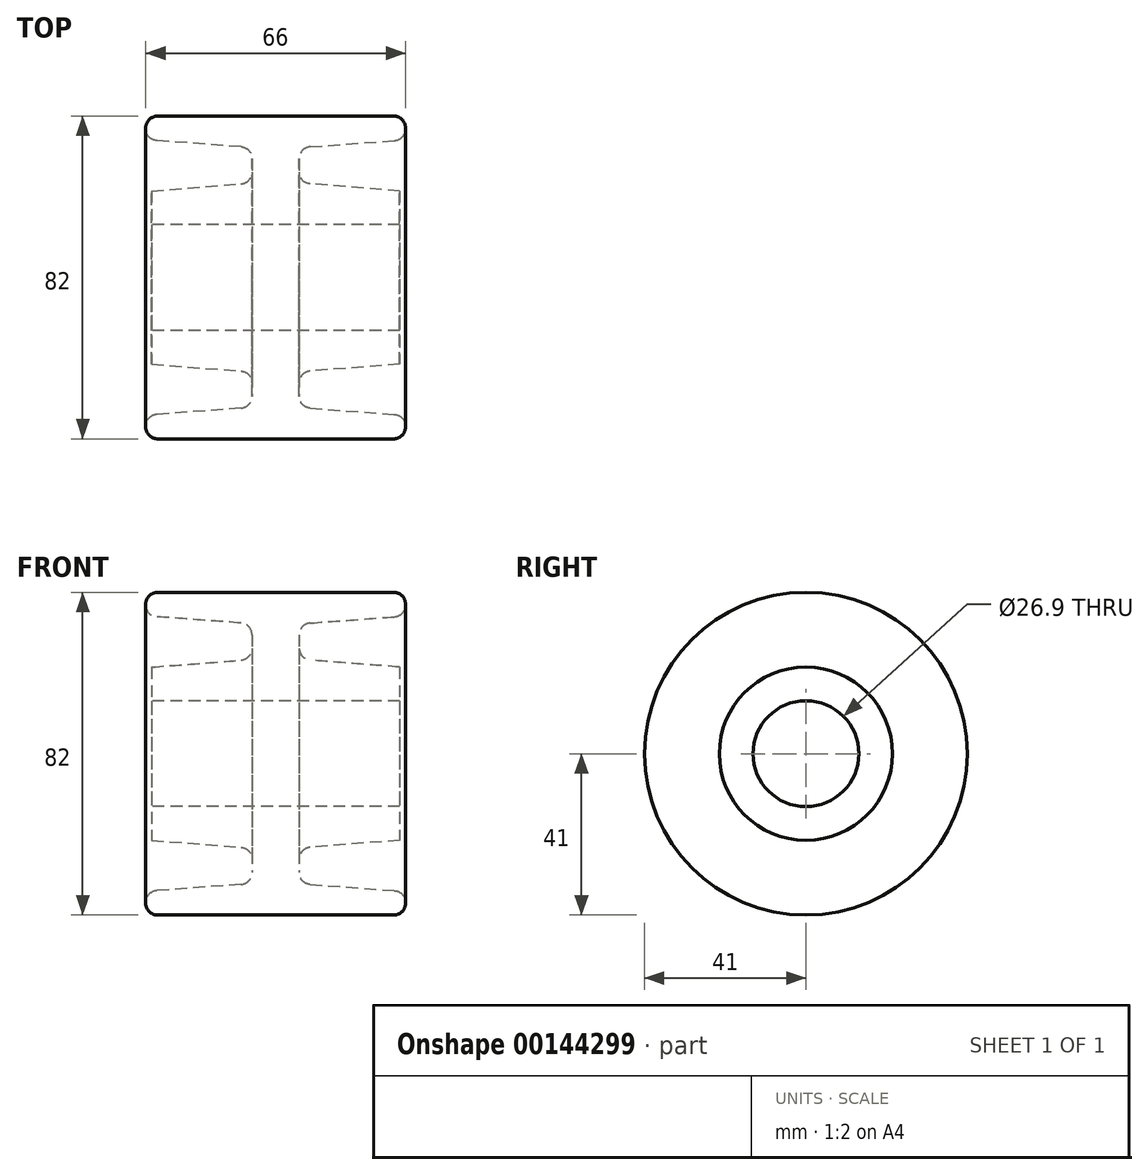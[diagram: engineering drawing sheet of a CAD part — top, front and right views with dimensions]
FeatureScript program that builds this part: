
annotation { "Feature Type Name" : "Feature", "Feature Type Description" : "" }
export const myFeature = defineFeature(function(context is Context, id is Id, definition is map)
    precondition{}
    {
        {
            var Q0;
            Q0=qCreatedBy(makeId("Front.planeOp"),FACE);
            var sketch = newSketch(context, id + "F0", { "sketchPlane" : qUnion([Q0])});
            skLineSegment(sketch, "E0", {"start": v(-24.5, 0) * mm, "end": v(76.5, 0) * mm, "construction": true});
            skLineSegment(sketch, "E1", {"start": v(64.5, 13.45) * mm, "end": v(64.5, 22) * mm});
            skLineSegment(sketch, "E2", {"start": v(64.5, 22) * mm, "end": v(41.77, 23.78) * mm});
            skLineSegment(sketch, "E3", {"start": v(39, 26.77) * mm, "end": v(39, 30.21) * mm});
            skLineSegment(sketch, "E4", {"start": v(66, 37.79) * mm, "end": v(66, 38) * mm});
            skLineSegment(sketch, "E5", {"start": v(63, 41) * mm, "end": v(3, 41) * mm});
            skLineSegment(sketch, "E6", {"start": v(27, 30.21) * mm, "end": v(27, 26.77) * mm});
            skLineSegment(sketch, "E7", {"start": v(24.23, 23.78) * mm, "end": v(1.5, 22) * mm});
            skLineSegment(sketch, "E8", {"start": v(1.5, 22) * mm, "end": v(1.5, 13.45) * mm});
            skLineSegment(sketch, "E9", {"start": v(1.5, 13.45) * mm, "end": v(64.5, 13.45) * mm});
            skLineSegment(sketch, "E10", {"start": v(33, 42.82) * mm, "end": v(33, -16.3) * mm, "construction": true});
            skLineSegment(sketch, "E11", {"start": v(0, 37.79) * mm, "end": v(0, 38) * mm});
            skLineSegment(sketch, "E12", {"start": v(2.78, 34.8) * mm, "end": v(24.22, 33.2) * mm});
            skLineSegment(sketch, "E13", {"start": v(41.78, 33.2) * mm, "end": v(63.22, 34.8) * mm});
            skPoint(sketch, "E14.visualSharp", {"position": v(0, 35) * mm});
            skArc(sketch, "E14.filletArc", {"start": v(0, 37.79) * mm, "mid": v(0.8, 35.74) * mm, "end": v(2.78, 34.8) * mm});
            skPoint(sketch, "E15.visualSharp", {"position": v(66, 35) * mm});
            skArc(sketch, "E15.filletArc", {"start": v(63.22, 34.8) * mm, "mid": v(65.2, 35.74) * mm, "end": v(66, 37.79) * mm});
            skPoint(sketch, "E16.visualSharp", {"position": v(27, 33) * mm});
            skArc(sketch, "E16.filletArc", {"start": v(27, 30.21) * mm, "mid": v(26.2, 32.26) * mm, "end": v(24.22, 33.2) * mm});
            skPoint(sketch, "E17.visualSharp", {"position": v(39, 33) * mm});
            skArc(sketch, "E17.filletArc", {"start": v(41.78, 33.2) * mm, "mid": v(39.8, 32.26) * mm, "end": v(39, 30.21) * mm});
            skPoint(sketch, "E18.visualSharp", {"position": v(27, 24) * mm});
            skArc(sketch, "E18.filletArc", {"start": v(24.23, 23.78) * mm, "mid": v(26.2, 24.74) * mm, "end": v(27, 26.77) * mm});
            skPoint(sketch, "E19.visualSharp", {"position": v(39, 24) * mm});
            skArc(sketch, "E19.filletArc", {"start": v(39, 26.77) * mm, "mid": v(39.8, 24.74) * mm, "end": v(41.77, 23.78) * mm});
            skPoint(sketch, "E20.visualSharp", {"position": v(0, 41) * mm});
            skArc(sketch, "E20.filletArc", {"start": v(3, 41) * mm, "mid": v(0.88, 40.12) * mm, "end": v(0, 38) * mm});
            skPoint(sketch, "E21.visualSharp", {"position": v(66, 41) * mm});
            skArc(sketch, "E21.filletArc", {"start": v(66, 38) * mm, "mid": v(65.12, 40.12) * mm, "end": v(63, 41) * mm});
            skSolve(sketch);
        }
        {
            var Q0;
            Q0=makeQuery(id+"F0.imprint","IMPRINT",FACE,{"disambiguationData":[TD([[makeQuery(id+"F0.imprint","IMPRINT",EDGE,{"derivedFrom":sQuery(id+"F0.wireOp",EDGE,"E1")}),1.0]])]});
            var Q1;
            Q1=sQuery(id+"F0.wireOp",EDGE,"E0");
            revolve(context, id + "F1", {"entities" : qUnion([Q0]), "axis" : qUnion([Q1]), "revolveType" : RevolveType.FULL});
        }
    });
